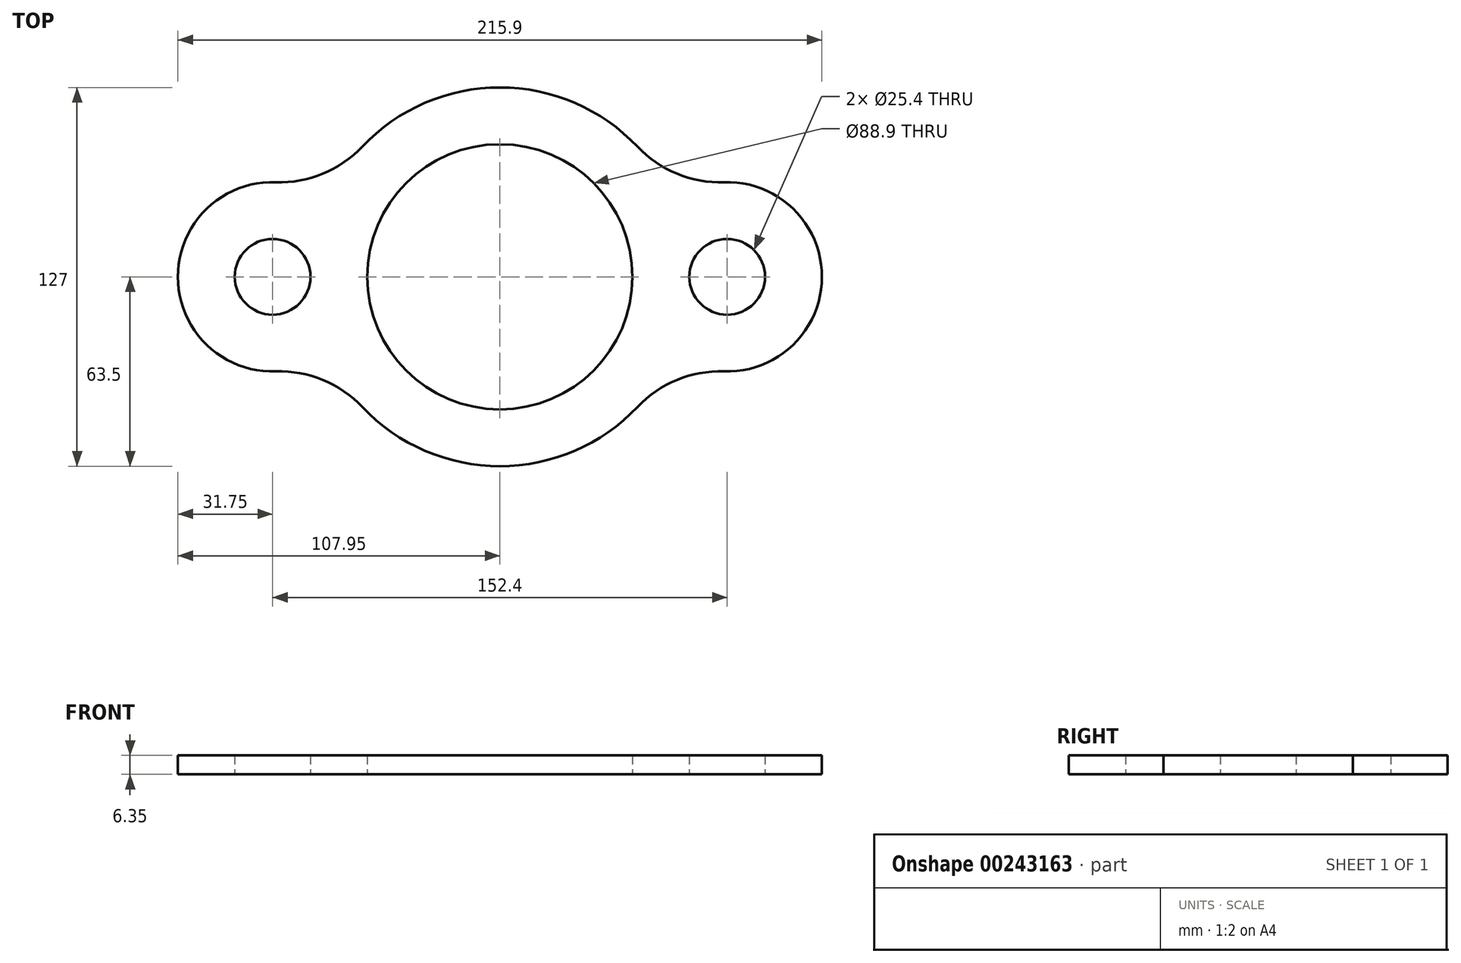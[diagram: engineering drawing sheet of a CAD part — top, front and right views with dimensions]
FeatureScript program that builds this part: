
annotation { "Feature Type Name" : "Feature", "Feature Type Description" : "" }
export const myFeature = defineFeature(function(context is Context, id is Id, definition is map)
    precondition{}
    {
        {
            var Q0;
            Q0=qCreatedBy(makeId("Top.planeOp"),FACE);
            var sketch = newSketch(context, id + "F0", { "sketchPlane" : qUnion([Q0])});
            skCircle(sketch, "E0", {"center": v(0, 0) * mm, "radius": 44.45 * mm});
            skCircle(sketch, "E1", {"center": v(-76.2, 0) * mm, "radius": 12.7 * mm});
            skCircle(sketch, "E2", {"center": v(76.2, 0) * mm, "radius": 12.7 * mm});
            skArc(sketch, "E3", {"start": v(-46.14, -43.63) * mm, "mid": v(0, -63.5) * mm, "end": v(46.14, -43.63) * mm});
            skArc(sketch, "E4", {"start": v(-75.12, 31.73) * mm, "mid": v(-107.95, 0) * mm, "end": v(-75.12, -31.73) * mm});
            skArc(sketch, "E5", {"start": v(75.12, -31.73) * mm, "mid": v(107.95, 0) * mm, "end": v(75.12, 31.73) * mm});
            skArc(sketch, "E6.trimOffspring", {"start": v(46.14, 43.63) * mm, "mid": v(0, 63.5) * mm, "end": v(-46.14, 43.63) * mm});
            skPoint(sketch, "E7.visualSharp", {"position": v(-57.94, 25.98) * mm});
            skArc(sketch, "E7.filletArc", {"start": v(-75.12, 31.73) * mm, "mid": v(-59.35, 34.56) * mm, "end": v(-46.14, 43.63) * mm});
            skPoint(sketch, "E8.visualSharp", {"position": v(57.94, 25.98) * mm});
            skArc(sketch, "E8.filletArc", {"start": v(46.14, 43.63) * mm, "mid": v(59.35, 34.56) * mm, "end": v(75.12, 31.73) * mm});
            skPoint(sketch, "E9.visualSharp", {"position": v(-57.94, -25.98) * mm});
            skArc(sketch, "E9.filletArc", {"start": v(-46.14, -43.63) * mm, "mid": v(-59.35, -34.56) * mm, "end": v(-75.12, -31.73) * mm});
            skPoint(sketch, "E10.visualSharp", {"position": v(57.94, -25.98) * mm});
            skArc(sketch, "E10.filletArc", {"start": v(75.12, -31.73) * mm, "mid": v(59.35, -34.56) * mm, "end": v(46.14, -43.63) * mm});
            skSolve(sketch);
        }
        {
            var Q0;
            Q0=makeQuery(id+"F0.imprint","IMPRINT",FACE,{"disambiguationData":[TD([[makeQuery(id+"F0.imprint","IMPRINT",EDGE,{"derivedFrom":sQuery(id+"F0.wireOp",EDGE,"E0")}),-1.0]])]});
            extrude(context, id + "F1", {"entities" : qUnion([Q0]), "depth" : 6.35 * mm});
        }
    });
